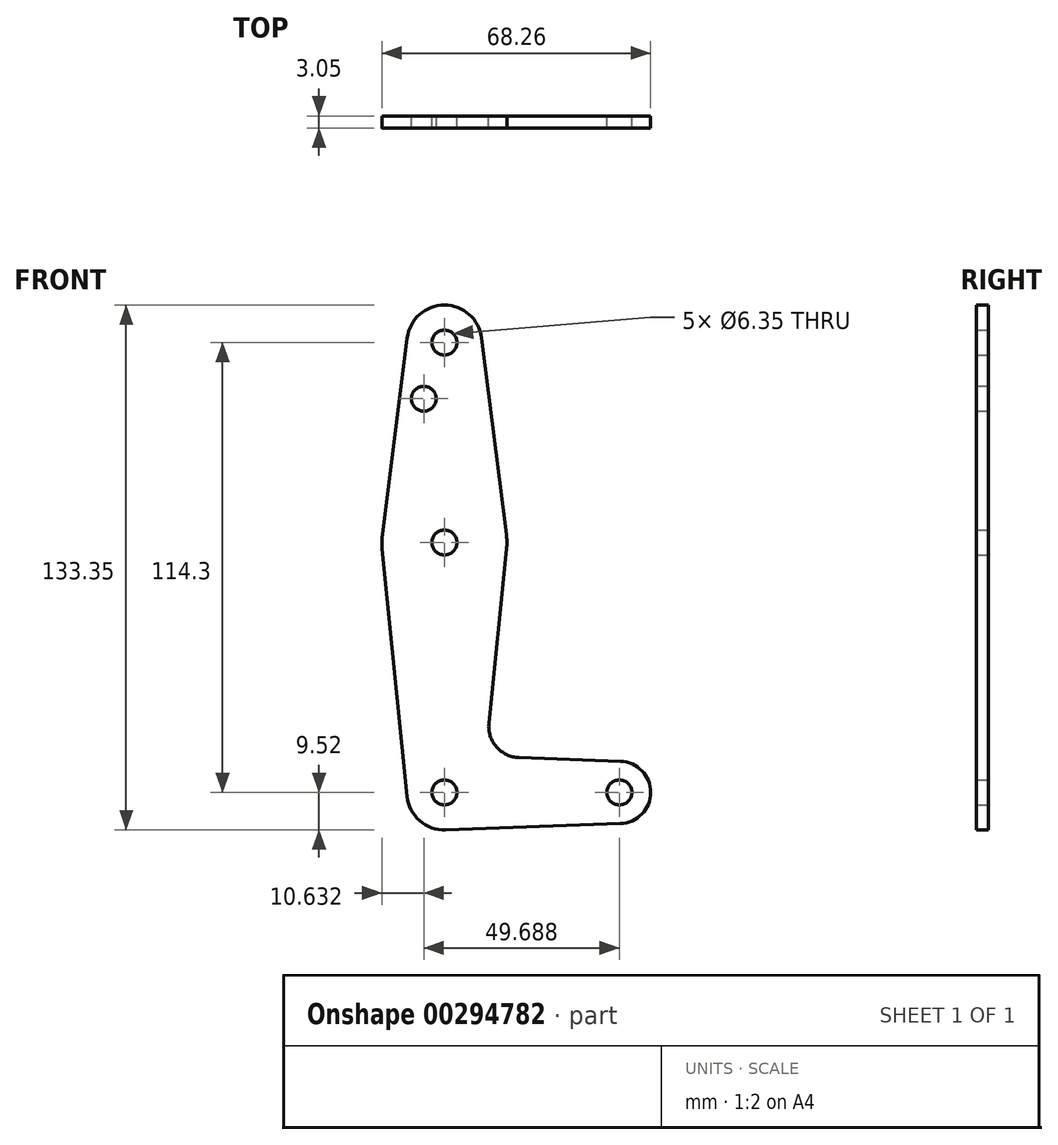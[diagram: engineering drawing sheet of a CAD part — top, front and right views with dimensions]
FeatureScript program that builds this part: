
annotation { "Feature Type Name" : "Feature", "Feature Type Description" : "" }
export const myFeature = defineFeature(function(context is Context, id is Id, definition is map)
    precondition{}
    {
        {
            var Q0;
            Q0=qCreatedBy(makeId("Front.planeOp"),FACE);
            var sketch = newSketch(context, id + "F0", { "sketchPlane" : qUnion([Q0])});
            skCircle(sketch, "E0", {"center": v(0, 0) * mm, "radius": 9.53 * mm});
            skCircle(sketch, "E1", {"center": v(44.45, 0) * mm, "radius": 7.94 * mm});
            skCircle(sketch, "E2", {"center": v(0, 63.5) * mm, "radius": 15.88 * mm});
            skCircle(sketch, "E3", {"center": v(0, 114.3) * mm, "radius": 9.53 * mm});
            skLineSegment(sketch, "E4", {"start": v(0, 0) * mm, "end": v(44.45, 0) * mm});
            skLineSegment(sketch, "E5", {"start": v(0, 0) * mm, "end": v(0, 63.5) * mm});
            skLineSegment(sketch, "E6", {"start": v(0, 63.5) * mm, "end": v(0, 114.3) * mm});
            skLineSegment(sketch, "E7", {"start": v(-9.45, 115.5) * mm, "end": v(-15.75, 65.48) * mm});
            skLineSegment(sketch, "E8", {"start": v(-15.8, 61.91) * mm, "end": v(-9.48, -0.95) * mm});
            skLineSegment(sketch, "E9", {"start": v(9.45, 115.5) * mm, "end": v(15.75, 65.48) * mm});
            skLineSegment(sketch, "E10", {"start": v(15.8, 61.9) * mm, "end": v(11.3, 17.6) * mm});
            skLineSegment(sketch, "E11", {"start": v(44.73, -7.93) * mm, "end": v(0.34, -9.52) * mm});
            skLineSegment(sketch, "E12", {"start": v(44.73, 7.93) * mm, "end": v(18.93, 8.85) * mm});
            skCircle(sketch, "E13", {"center": v(0, 114.3) * mm, "radius": 3.18 * mm});
            skCircle(sketch, "E14", {"center": v(0, 63.5) * mm, "radius": 3.18 * mm});
            skCircle(sketch, "E15", {"center": v(0, 0) * mm, "radius": 3.18 * mm});
            skCircle(sketch, "E16", {"center": v(44.45, 0) * mm, "radius": 3.18 * mm});
            skCircle(sketch, "E17", {"center": v(-5.24, 100.03) * mm, "radius": 3.18 * mm});
            skArc(sketch, "E18.filletArc", {"start": v(11.3, 17.6) * mm, "mid": v(13.22, 11.57) * mm, "end": v(18.93, 8.85) * mm});
            skSolve(sketch);
        }
        {
            var Q0;
            Q0=makeQuery(id+"F0.imprint","IMPRINT",FACE,{"disambiguationData":[TD([[makeQuery(id+"F0.imprint","IMPRINT",EDGE,{"derivedFrom":sQuery(id+"F0.wireOp",EDGE,"E13")}),-1.0]])]});
            var Q1;
            {var subQ0=sQuery(id+"F0.wireOp",EDGE,"E7");Q1=makeQuery(id+"F0.imprint","IMPRINT",FACE,{"disambiguationData":[TD([[makeQuery(id+"F0.imprint","IMPRINT",EDGE,{"derivedFrom":subQ0}),1.0]])]});}
            var Q2;
            {var subQ0=sQuery(id+"F0.wireOp",EDGE,"E9");Q2=makeQuery(id+"F0.imprint","IMPRINT",FACE,{"disambiguationData":[TD([[makeQuery(id+"F0.imprint","IMPRINT",EDGE,{"derivedFrom":subQ0}),-1.0]])]});}
            var Q3;
            {var subQ1=sQuery(id+"F0.wireOp",EDGE,"E2");var subQ6=makeQuery(id+"F0.imprint","INTERSECT",VERTEX,{"derivedFrom":[subQ1,sQuery(id+"F0.wireOp",EDGE,"E7")]});Q3=makeQuery(id+"F0.imprint","IMPRINT",FACE,{"disambiguationData":[TD([[makeQuery(id+"F0.imprint","IMPRINT",EDGE,{"disambiguationData":[TD([[subQ6,1.0]])],"derivedFrom":subQ1}),1.0]])]});}
            var Q4;
            {var subQ0=sQuery(id+"F0.wireOp",EDGE,"E2");var subQ6=makeQuery(id+"F0.imprint","INTERSECT",VERTEX,{"derivedFrom":[subQ0,sQuery(id+"F0.wireOp",EDGE,"E9")]});Q4=makeQuery(id+"F0.imprint","IMPRINT",FACE,{"disambiguationData":[TD([[makeQuery(id+"F0.imprint","IMPRINT",EDGE,{"disambiguationData":[TD([[subQ6,-1.0]])],"derivedFrom":subQ0}),1.0]])]});}
            var Q5;
            {var subQ0=sQuery(id+"F0.wireOp",EDGE,"E8");Q5=makeQuery(id+"F0.imprint","IMPRINT",FACE,{"disambiguationData":[TD([[makeQuery(id+"F0.imprint","IMPRINT",EDGE,{"derivedFrom":subQ0}),1.0]])]});}
            var Q6;
            {var subQ5=sQuery(id+"F0.wireOp",EDGE,"E10");Q6=makeQuery(id+"F0.imprint","IMPRINT",FACE,{"disambiguationData":[TD([[makeQuery(id+"F0.imprint","IMPRINT",EDGE,{"derivedFrom":subQ5}),-1.0]])]});}
            var Q7;
            {var subQ0=sQuery(id+"F0.wireOp",EDGE,"E0");var subQ6=makeQuery(id+"F0.imprint","INTERSECT",VERTEX,{"derivedFrom":[subQ0,sQuery(id+"F0.wireOp",EDGE,"E8")]});Q7=makeQuery(id+"F0.imprint","IMPRINT",FACE,{"disambiguationData":[TD([[makeQuery(id+"F0.imprint","IMPRINT",EDGE,{"disambiguationData":[TD([[subQ6,1.0]])],"derivedFrom":subQ0}),1.0]])]});}
            var Q8;
            {var subQ0=sQuery(id+"F0.wireOp",EDGE,"E5");var subQ1=sQuery(id+"F0.wireOp",EDGE,"E0");var subQ2=makeQuery(id+"F0.imprint","INTERSECT",VERTEX,{"derivedFrom":[subQ1,subQ0]});Q8=makeQuery(id+"F0.imprint","IMPRINT",FACE,{"disambiguationData":[TD([[makeQuery(id+"F0.imprint","IMPRINT",EDGE,{"disambiguationData":[TD([[subQ2,1.0]])],"derivedFrom":subQ1}),1.0]])]});}
            var Q9;
            {var subQ0=sQuery(id+"F0.wireOp",EDGE,"E11");Q9=makeQuery(id+"F0.imprint","IMPRINT",FACE,{"disambiguationData":[TD([[makeQuery(id+"F0.imprint","IMPRINT",EDGE,{"derivedFrom":subQ0}),-1.0]])]});}
            var Q10;
            Q10=makeQuery(id+"F0.imprint","IMPRINT",FACE,{"disambiguationData":[TD([[makeQuery(id+"F0.imprint","IMPRINT",EDGE,{"derivedFrom":sQuery(id+"F0.wireOp",EDGE,"E16")}),-1.0]])]});
            extrude(context, id + "F1", {"entities" : qUnion([Q0, Q1, Q2, Q3, Q4, Q5, Q6, Q7, Q8, Q9, Q10]), "depth" : 3.05 * mm});
        }
    });
